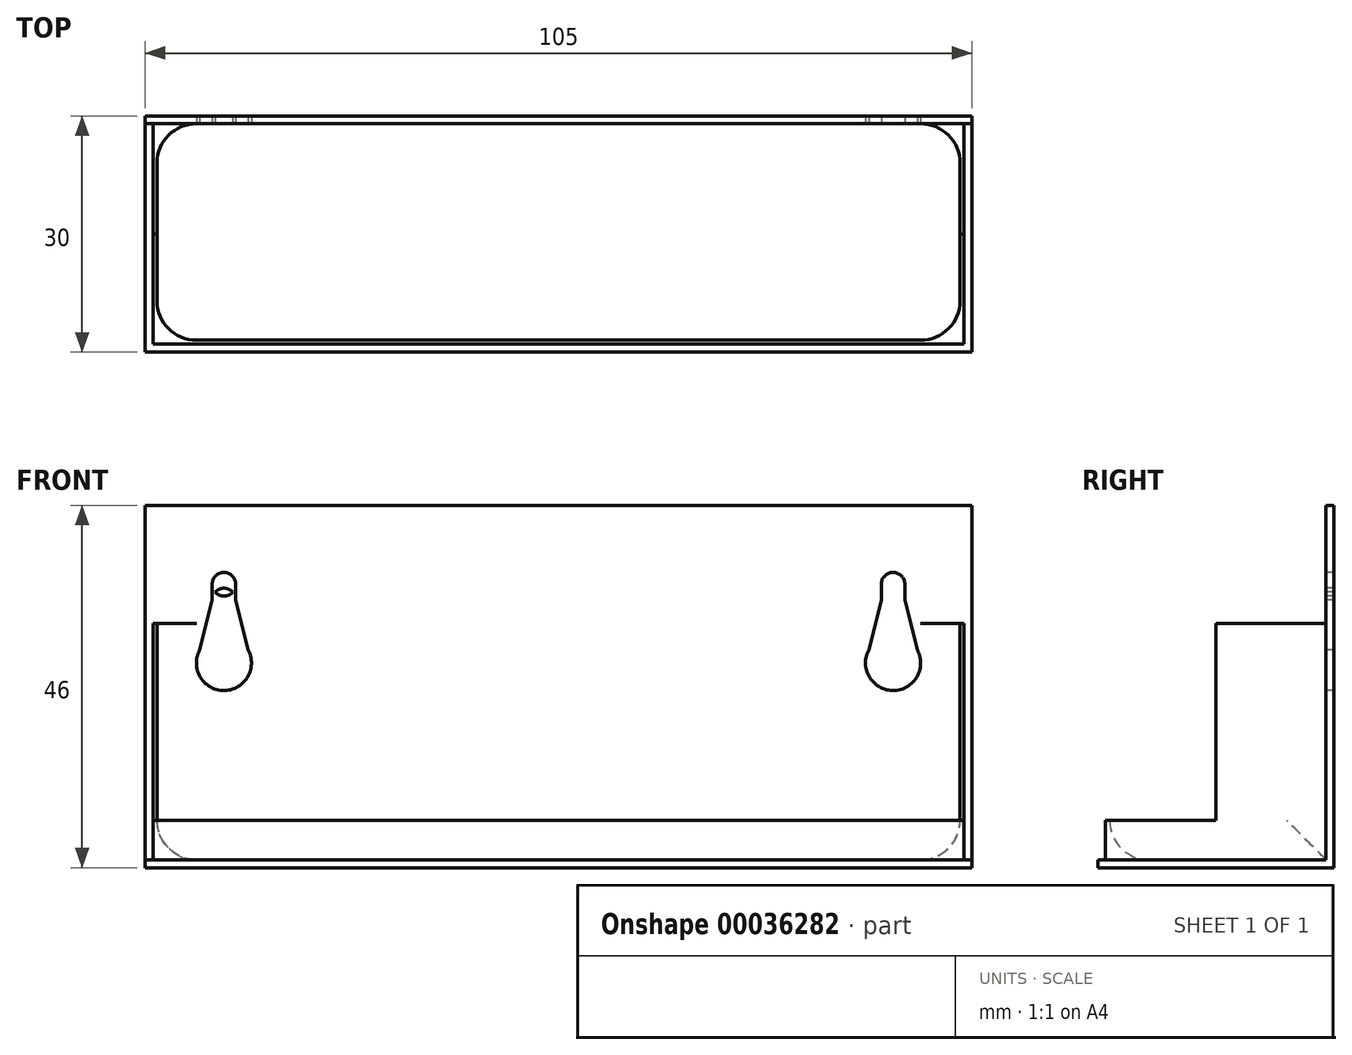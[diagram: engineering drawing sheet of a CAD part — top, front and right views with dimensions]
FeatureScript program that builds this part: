
annotation { "Feature Type Name" : "Feature", "Feature Type Description" : "" }
export const myFeature = defineFeature(function(context is Context, id is Id, definition is map)
    precondition{}
    {
        {
            var Q0;
            Q0=qCreatedBy(makeId("Top.planeOp"),FACE);
            var sketch = newSketch(context, id + "F0", { "sketchPlane" : qUnion([Q0])});
            skLineSegment(sketch, "E0.bottom", {"start": v(0, 0) * mm, "end": v(105, 0) * mm});
            skLineSegment(sketch, "E0.top", {"start": v(0, -30) * mm, "end": v(105, -30) * mm});
            skLineSegment(sketch, "E0.left", {"start": v(0, 0) * mm, "end": v(0, -30) * mm});
            skLineSegment(sketch, "E0.right", {"start": v(105, 0) * mm, "end": v(105, -30) * mm});
            skLineSegment(sketch, "E1.0", {"start": v(1, -1) * mm, "end": v(104, -1) * mm});
            skLineSegment(sketch, "E1.1", {"start": v(1, -1) * mm, "end": v(1, -29) * mm});
            skLineSegment(sketch, "E1.2", {"start": v(1, -29) * mm, "end": v(104, -29) * mm});
            skLineSegment(sketch, "E1.3", {"start": v(104, -1) * mm, "end": v(104, -29) * mm});
            skLineSegment(sketch, "E2.0", {"start": v(103.5, -1) * mm, "end": v(103.5, -28.5) * mm});
            skLineSegment(sketch, "E2.1", {"start": v(1.5, -28.5) * mm, "end": v(103.5, -28.5) * mm});
            skLineSegment(sketch, "E2.2", {"start": v(1.5, -1) * mm, "end": v(1.5, -28.5) * mm});
            skLineSegment(sketch, "E3", {"start": v(1, -1) * mm, "end": v(0, -1) * mm});
            skLineSegment(sketch, "E4", {"start": v(104, -1) * mm, "end": v(105, -1) * mm});
            skSolve(sketch);
        }
        {
            var Q0;
            {var subQ2=sQuery(id+"F0.wireOp",EDGE,"E2.1");Q0=makeQuery(id+"F0.imprint","IMPRINT",FACE,{"disambiguationData":[TD([[makeQuery(id+"F0.imprint","IMPRINT",EDGE,{"derivedFrom":subQ2}),1.0]])]});}
            var Q1;
            {var subQ5=sQuery(id+"F0.wireOp",EDGE,"E1.2");Q1=makeQuery(id+"F0.imprint","IMPRINT",FACE,{"disambiguationData":[TD([[makeQuery(id+"F0.imprint","IMPRINT",EDGE,{"derivedFrom":subQ5}),1.0]])]});}
            var Q2;
            {var subQ9=sQuery(id+"F0.wireOp",EDGE,"E0.top");Q2=makeQuery(id+"F0.imprint","IMPRINT",FACE,{"disambiguationData":[TD([[makeQuery(id+"F0.imprint","IMPRINT",EDGE,{"derivedFrom":subQ9}),1.0]])]});}
            var Q3;
            {var subQ0=sQuery(id+"F0.wireOp",EDGE,"b7d10d21-684f-4088-a917-c518dc741e65");Q3=makeQuery(id+"F0.imprint","IMPRINT",FACE,{"disambiguationData":[TD([[makeQuery(id+"F0.imprint","IMPRINT",EDGE,{"derivedFrom":subQ0}),1.0]])]});}
            var Q4;
            {var subQ6=sQuery(id+"F0.wireOp",EDGE,"E0.bottom");Q4=makeQuery(id+"F0.imprint","IMPRINT",FACE,{"disambiguationData":[TD([[makeQuery(id+"F0.imprint","IMPRINT",EDGE,{"derivedFrom":subQ6}),-1.0]])]});}
            var Q5;
            {var subQ0=sQuery(id+"F0.wireOp",EDGE,"48654bb7-be4e-45c6-be64-ad9a2630f81e");Q5=makeQuery(id+"F0.imprint","IMPRINT",FACE,{"disambiguationData":[TD([[makeQuery(id+"F0.imprint","IMPRINT",EDGE,{"derivedFrom":subQ0}),-1.0]])]});}
            extrude(context, id + "F1", {"entities" : qUnion([Q0, Q1, Q2, Q3, Q4, Q5]), "oppositeDirection" : true, "depth" : 1 * mm});
        }
        {
            var Q0;
            {var subQ0=sQuery(id+"F0.wireOp",EDGE,"48654bb7-be4e-45c6-be64-ad9a2630f81e");Q0=makeQuery(id+"F0.imprint","IMPRINT",FACE,{"disambiguationData":[TD([[makeQuery(id+"F0.imprint","IMPRINT",EDGE,{"derivedFrom":subQ0}),-1.0]])]});}
            var Q1;
            {var subQ6=sQuery(id+"F0.wireOp",EDGE,"E0.bottom");Q1=makeQuery(id+"F0.imprint","IMPRINT",FACE,{"disambiguationData":[TD([[makeQuery(id+"F0.imprint","IMPRINT",EDGE,{"derivedFrom":subQ6}),-1.0]])]});}
            var Q2;
            {var subQ5=sQuery(id+"F0.wireOp",EDGE,"E1.2");Q2=makeQuery(id+"F0.imprint","IMPRINT",FACE,{"disambiguationData":[TD([[makeQuery(id+"F0.imprint","IMPRINT",EDGE,{"derivedFrom":subQ5}),1.0]])]});}
            var Q3;
            {var subQ0=sQuery(id+"F0.wireOp",EDGE,"b7d10d21-684f-4088-a917-c518dc741e65");Q3=makeQuery(id+"F0.imprint","IMPRINT",FACE,{"disambiguationData":[TD([[makeQuery(id+"F0.imprint","IMPRINT",EDGE,{"derivedFrom":subQ0}),1.0]])]});}
            extrude(context, id + "F2", {"entities" : qUnion([Q0, Q1, Q2, Q3]), "operationType" : NewBodyOperationType.ADD, "depth" : 5 * mm});
        }
        {
            var Q0;
            Q0=makeQuery(id+"F2.opExtrude","CAP_FACE",FACE,{"disambiguationData":[OSD([sQuery(id+"F0.wireOp",EDGE,"E0.bottom"),sQuery(id+"F0.wireOp",EDGE,"E0.left"),sQuery(id+"F0.wireOp",EDGE,"E0.right"),sQuery(id+"F0.wireOp",EDGE,"E1.0"),sQuery(id+"F0.wireOp",EDGE,"E1.1"),sQuery(id+"F0.wireOp",EDGE,"E1.2"),sQuery(id+"F0.wireOp",EDGE,"E1.3"),sQuery(id+"F0.wireOp",EDGE,"E2.0"),sQuery(id+"F0.wireOp",EDGE,"E2.1"),sQuery(id+"F0.wireOp",EDGE,"E2.2"),sQuery(id+"F0.wireOp",EDGE,"E3"),sQuery(id+"F0.wireOp",EDGE,"E4")])],"isStart":false});
            var sketch = newSketch(context, id + "F3", { "sketchPlane" : qUnion([Q0])});
            skLineSegment(sketch, "E5", {"start": v(1, -15) * mm, "end": v(1.5, -15) * mm});
            skLineSegment(sketch, "E6", {"start": v(104, -15) * mm, "end": v(103.5, -15) * mm});
            skSolve(sketch);
        }
        {
            var Q0;
            {var subQ6=sQuery(id+"F3.wireOp",EDGE,"E5");Q0=makeQuery(id+"F3.imprint","IMPRINT",FACE,{"disambiguationData":[TD([[makeQuery(id+"F3.imprint","IMPRINT",EDGE,{"derivedFrom":subQ6}),1.0]])]});}
            extrude(context, id + "F4", {"entities" : qUnion([Q0]), "operationType" : NewBodyOperationType.ADD, "depth" : 25 * mm});
        }
        {
            var Q0;
            Q0=makeQuery(id+"F4.opExtrude","CAP_FACE",FACE,{"disambiguationData":[OSD([sQuery(id+"F0.wireOp",EDGE,"E0.bottom"),sQuery(id+"F0.wireOp",EDGE,"E0.left"),sQuery(id+"F0.wireOp",EDGE,"E0.right"),sQuery(id+"F0.wireOp",EDGE,"E1.0"),sQuery(id+"F0.wireOp",EDGE,"E1.1"),sQuery(id+"F0.wireOp",EDGE,"E1.3"),sQuery(id+"F0.wireOp",EDGE,"E2.0"),sQuery(id+"F0.wireOp",EDGE,"E2.2"),sQuery(id+"F0.wireOp",EDGE,"E3"),sQuery(id+"F0.wireOp",EDGE,"E4"),sQuery(id+"F3.wireOp",EDGE,"E5"),sQuery(id+"F3.wireOp",EDGE,"E6")])],"isStart":false});
            var sketch = newSketch(context, id + "F5", { "sketchPlane" : qUnion([Q0])});
            skLineSegment(sketch, "E7", {"start": v(103.5, -1) * mm, "end": v(104, -1) * mm});
            skLineSegment(sketch, "E8", {"start": v(1, -1) * mm, "end": v(1.5, -1) * mm});
            skSolve(sketch);
        }
        {
            var Q0;
            Q0=qSketchRegion(id+"F5",true);
            var Q1;
            Q1=makeQuery(id+"F5.imprint","IMPRINT",FACE,{"disambiguationData":[TD([[makeQuery(id+"F5.imprint","IMPRINT",EDGE,{"derivedFrom":sQuery(id+"F5.wireOp",EDGE,"E7")}),1.0]])]});
            extrude(context, id + "F6", {"entities" : qUnion([Q0, Q1]), "operationType" : NewBodyOperationType.ADD, "depth" : 15 * mm});
        }
        {
            var Q0;
            {var subQ0=sQuery(id+"F0.wireOp",EDGE,"E1.0");var subQ1=sQuery(id+"F0.wireOp",EDGE,"E3");var subQ2=sQuery(id+"F0.wireOp",EDGE,"E4");Q0=makeQuery(id+"F6.boolean.opBoolean","MERGE",FACE,{"derivedFrom":[makeQuery(id+"F4.boolean.opBoolean","MERGE",FACE,{"derivedFrom":[makeQuery(id+"F2.opExtrude","SWEPT_FACE",FACE,{"disambiguationData":[OSD([subQ0])]}),makeQuery(id+"F4.opExtrude","SWEPT_FACE",FACE,{"disambiguationData":[OSD([subQ0])]})]}),makeQuery(id+"F4.boolean.opBoolean","MERGE",FACE,{"derivedFrom":[makeQuery(id+"F2.opExtrude","SWEPT_FACE",FACE,{"disambiguationData":[OSD([subQ1])]}),makeQuery(id+"F4.opExtrude","SWEPT_FACE",FACE,{"disambiguationData":[OSD([subQ1])]})]}),makeQuery(id+"F4.boolean.opBoolean","MERGE",FACE,{"derivedFrom":[makeQuery(id+"F2.opExtrude","SWEPT_FACE",FACE,{"disambiguationData":[OSD([subQ2])]}),makeQuery(id+"F4.opExtrude","SWEPT_FACE",FACE,{"disambiguationData":[OSD([subQ2])]})]}),makeQuery(id+"F6.opExtrude","SWEPT_FACE",FACE,{"disambiguationData":[OSD([subQ0,subQ1,subQ2,sQuery(id+"F5.wireOp",EDGE,"E7"),sQuery(id+"F5.wireOp",EDGE,"E8")])]})]});}
            var sketch = newSketch(context, id + "F7", { "sketchPlane" : qUnion([Q0])});
            skCircle(sketch, "E9", {"center": v(10, 25) * mm, "radius": 3.5 * mm});
            skCircle(sketch, "E10", {"center": v(10, 35) * mm, "radius": 1.5 * mm});
            skCircle(sketch, "E11", {"center": v(10, 33) * mm, "radius": 1.5 * mm});
            skLineSegment(sketch, "E12", {"start": v(11.5, 33) * mm, "end": v(11.5, 35) * mm});
            skLineSegment(sketch, "E13", {"start": v(11.5, 35) * mm, "end": v(8.5, 35) * mm});
            skLineSegment(sketch, "E14", {"start": v(8.5, 35) * mm, "end": v(8.5, 33) * mm});
            skLineSegment(sketch, "E15", {"start": v(8.5, 33) * mm, "end": v(6.5, 25) * mm});
            skLineSegment(sketch, "E16", {"start": v(6.5, 25) * mm, "end": v(13.5, 25) * mm});
            skLineSegment(sketch, "E17", {"start": v(13.5, 25) * mm, "end": v(11.5, 33) * mm});
            skCircle(sketch, "E18", {"center": v(95, 25) * mm, "radius": 3.5 * mm});
            skCircle(sketch, "E19", {"center": v(95, 33) * mm, "radius": 1.5 * mm});
            skCircle(sketch, "E20", {"center": v(95, 35) * mm, "radius": 1.5 * mm});
            skLineSegment(sketch, "E21", {"start": v(98.5, 25) * mm, "end": v(96.5, 33) * mm});
            skLineSegment(sketch, "E22", {"start": v(96.5, 33) * mm, "end": v(96.5, 35) * mm});
            skLineSegment(sketch, "E23", {"start": v(93.5, 35) * mm, "end": v(93.5, 33) * mm});
            skLineSegment(sketch, "E24", {"start": v(93.5, 33) * mm, "end": v(91.5, 25) * mm});
            skSolve(sketch);
        }
        {
            var Q0;
            Q0=qSketchRegion(id+"F7",true);
            var Q1;
            {var subQ0=sQuery(id+"F7.wireOp",EDGE,"E11");var subQ3=sQuery(id+"F7.wireOp",EDGE,"E10");var subQ4=makeQuery(id+"F7.imprint","INTERSECT",VERTEX,{"disambiguationData":[OD(0.0)],"derivedFrom":[subQ3,subQ0]});Q1=makeQuery(id+"F7.imprint","IMPRINT",FACE,{"disambiguationData":[TD([[makeQuery(id+"F7.imprint","IMPRINT",EDGE,{"disambiguationData":[TD([[subQ4,-1.0]])],"derivedFrom":subQ3}),-1.0]])]});}
            var Q2;
            {var subQ0=sQuery(id+"F7.wireOp",EDGE,"E11");var subQ1=sQuery(id+"F7.wireOp",EDGE,"E10");var subQ3=makeQuery(id+"F7.imprint","INTERSECT",VERTEX,{"disambiguationData":[OD(0.0)],"derivedFrom":[subQ1,subQ0]});Q2=makeQuery(id+"F7.imprint","IMPRINT",FACE,{"disambiguationData":[TD([[makeQuery(id+"F7.imprint","IMPRINT",EDGE,{"disambiguationData":[TD([[subQ3,-1.0]])],"derivedFrom":subQ1}),1.0]])]});}
            var Q3;
            {var subQ0=sQuery(id+"F7.wireOp",EDGE,"E13");Q3=makeQuery(id+"F7.imprint","IMPRINT",FACE,{"disambiguationData":[TD([[makeQuery(id+"F7.imprint","IMPRINT",EDGE,{"derivedFrom":subQ0}),1.0]])]});}
            var Q4;
            {var subQ0=sQuery(id+"F7.wireOp",EDGE,"E20");var subQ1=sQuery(id+"F7.wireOp",EDGE,"E19");var subQ3=makeQuery(id+"F7.imprint","INTERSECT",VERTEX,{"disambiguationData":[OD(0.0)],"derivedFrom":[subQ1,subQ0]});Q4=makeQuery(id+"F7.imprint","IMPRINT",FACE,{"disambiguationData":[TD([[makeQuery(id+"F7.imprint","IMPRINT",EDGE,{"disambiguationData":[TD([[subQ3,1.0]])],"derivedFrom":subQ0}),-1.0]])]});}
            var Q5;
            {var subQ0=sQuery(id+"F7.wireOp",EDGE,"E20");var subQ1=sQuery(id+"F7.wireOp",EDGE,"E19");var subQ3=makeQuery(id+"F7.imprint","INTERSECT",VERTEX,{"disambiguationData":[OD(0.0)],"derivedFrom":[subQ1,subQ0]});Q5=makeQuery(id+"F7.imprint","IMPRINT",FACE,{"disambiguationData":[TD([[makeQuery(id+"F7.imprint","IMPRINT",EDGE,{"disambiguationData":[TD([[subQ3,-1.0]])],"derivedFrom":subQ1}),1.0]])]});}
            extrude(context, id + "F8", {"entities" : qUnion([Q0, Q1, Q2, Q3, Q4, Q5]), "operationType" : NewBodyOperationType.REMOVE, "endBound" : BoundingType.UP_TO_NEXT, "oppositeDirection" : true, "depth" : 25 * mm});
        }
        {
            var Q0;
            Q0=makeQuery(id+"F2.opExtrude","CAP_EDGE",EDGE,{"disambiguationData":[OSD([sQuery(id+"F0.wireOp",EDGE,"E2.2")])],"isStart":true});
            var Q1;
            Q1=makeQuery(id+"F2.opExtrude","CAP_EDGE",EDGE,{"disambiguationData":[OSD([sQuery(id+"F0.wireOp",EDGE,"E2.0")])],"isStart":true});
            var Q2;
            {var subQ0=sQuery(id+"F0.wireOp",EDGE,"E1.0");var subQ1=sQuery(id+"F0.wireOp",EDGE,"E2.0");Q2=makeQuery(id+"F4.boolean.opBoolean","MERGE",EDGE,{"derivedFrom":[makeQuery(id+"F2.opExtrude","SWEPT_EDGE",EDGE,{"disambiguationData":[OSD([subQ0,subQ1])]}),makeQuery(id+"F4.opExtrude","SWEPT_EDGE",EDGE,{"disambiguationData":[OSD([subQ0,subQ1])]})]});}
            var Q3;
            {var subQ0=sQuery(id+"F0.wireOp",EDGE,"E1.0");var subQ1=sQuery(id+"F0.wireOp",EDGE,"E2.2");Q3=makeQuery(id+"F4.boolean.opBoolean","MERGE",EDGE,{"derivedFrom":[makeQuery(id+"F2.opExtrude","SWEPT_EDGE",EDGE,{"disambiguationData":[OSD([subQ0,subQ1])]}),makeQuery(id+"F4.opExtrude","SWEPT_EDGE",EDGE,{"disambiguationData":[OSD([subQ0,subQ1])]})]});}
            fillet(context, id + "F9", {"entities" : qUnion([Q0, Q1, Q2, Q3]), "radius" : 5 * mm, "tangentPropagation" : true, "allowEdgeOverflow" : false});
        }
        {
            var Q0;
            Q0=makeQuery(id+"F2.opExtrude","CAP_EDGE",EDGE,{"disambiguationData":[OSD([sQuery(id+"F0.wireOp",EDGE,"E2.1")])],"isStart":true});
            fillet(context, id + "F10", {"entities" : qUnion([Q0]), "radius" : 5 * mm, "tangentPropagation" : true, "allowEdgeOverflow" : false});
        }
    });
